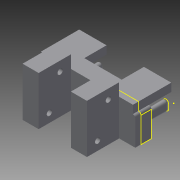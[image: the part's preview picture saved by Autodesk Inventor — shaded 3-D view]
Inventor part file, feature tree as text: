
AUTODESK INVENTOR PART (.ipt)
format: ipt  version: 2013 SP2 (Build 170200200, 200)  size: 309,248 bytes
history: native  units: in
note: dims shown in document units (in); Inventor stores cm internally (conversion verified against a paired STEP export)
features: other x20, sketch x17, extrude x14, fillet x1, mirror x1
ambient origin geometry x8: Origin, YZ Plane, XZ Plane, XY Plane, X Axis, Y Axis, Z Axis, Center Point
bodies: Solid2 (feature_tree)
feature tree (53):
  sketch  "Sketch1"  dims[d15=0.1437in d18=0.69in d19=-0.0069in]
  extrude  "Extrusion2"  Depth=0.69in
  extrude  "Extrusion3"  Depth=0.25in
  extrude  "Extrusion4"  Depth=0.06in
  sketch  "Sketch4"  dims[d35=0.174in d36=0.0in d37=0.25in d38=0.0in]
  fillet  "Fillet1"  Radius=0.076in
  extrude  "Extrusion5"  Depth=0.25in TaperAngle=0.0deg
  sketch  "Sketch7"  dims[d42=1.0in d43=0.0in d44=0.25in]
  sketch  "Sketch8"  dims[d45=1.0in d46=0.0in d56=0.5in]
  extrude  "Extrusion6"  Depth=0.25in
  extrude  "Extrusion7"  Depth=0.25in
  extrude  "Extrusion8"  Depth=0.5in
  extrude  "Extrusion9"  Depth=0.63in
  extrude  "Extrusion10"  Depth=0.395in
  extrude  "Extrusion12"  Depth=0.39in TaperAngle=0.0deg
  mirror  "Mirror1"
  extrude  "Extrusion13"  Depth=0.85in
  extrude  "Extrusion14"  Depth=0.27in
  extrude  "Extrusion15"  Depth=2.0in TaperAngle=0.0deg
  extrude  "Extrusion16"  [1 undecoded]
  sketch  "Sketch2"  dims[d25=0.25in d26=0.0in d27=0.25in]
  sketch  "Sketch3"  dims[d28=0.94in d29=0.0in d30=0.06in d31=0.076in d32=0.0in]
  sketch  "Sketch5"  dims[d39=0.25in d40=0.0in d41=0.25in]
  sketch  "Sketch9"  dims[d57=0.5in d58=0.0in d59=0.63in]
  sketch  "Sketch10"  dims[d60=0.06in d61=0.0in d62=0.395in]
  sketch  "Sketch11"  dims[d64=1.0in d65=0.0in d66=0.39in d67=0.0in]
  sketch  "Sketch12"  dims[d70=0.165in d71=0.85in]
  sketch  "Sketch13"  dims[d72=0.3333in d73=0.27in]
  sketch  "Sketch16"  dims[d74=0.165in d75=2.0in d76=0.0in]
  sketch  "Sketch17"
  sketch  "Sketch18"
  sketch  "Sketch19"
  sketch  "Sketch20"
  other  "Composite1"
  other  "Composite2"
  other  "Composite3"
  other  "Composite4"
  other  "Composite5"
  other  "Composite6"
  other  "Composite7"
  other  "Composite8"
  other  "Composite9"
  other  "Composite10"
  other  "Srf1"
  other  "Srf2"
  other  "Srf3"
  other  "Srf4"
  other  "Srf5"
  other  "Srf6"
  other  "Srf7"
  other  "Srf8"
  other  "Srf9"
  other  "Srf10"
note: 1 required parameter value undecoded (feature->parameter linkage not recoverable at this tier; creation-order binding heuristic only, values carry confidence <= 0.55)
